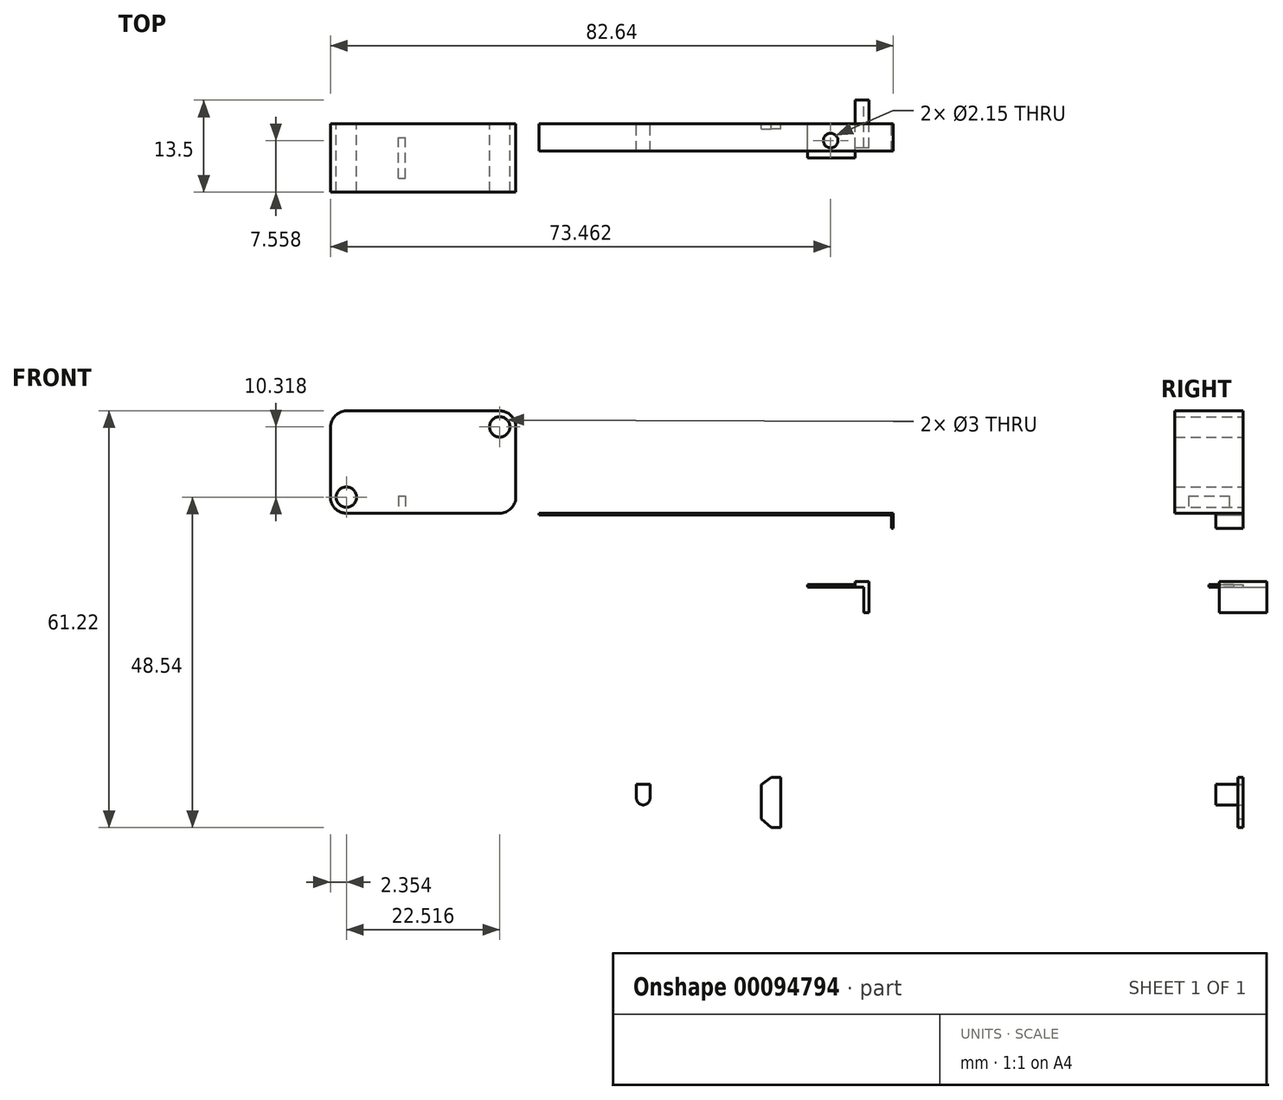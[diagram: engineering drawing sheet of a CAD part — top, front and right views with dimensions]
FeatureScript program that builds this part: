
annotation { "Feature Type Name" : "Feature", "Feature Type Description" : "" }
export const myFeature = defineFeature(function(context is Context, id is Id, definition is map)
    precondition{}
    {
        {
            var Q0;
            Q0=qCreatedBy(makeId("Front.planeOp"),FACE);
            var sketch = newSketch(context, id + "F0", { "sketchPlane" : qUnion([Q0])});
            skCircle(sketch, "E0", {"center": v(-20.95, 13.42) * mm, "radius": 2.36 * mm});
            skCircle(sketch, "E1", {"center": v(1.53, 13.43) * mm, "radius": 2.36 * mm});
            skCircle(sketch, "E2", {"center": v(-20.99, 3.11) * mm, "radius": 2.36 * mm});
            skCircle(sketch, "E3", {"center": v(1.53, 3.11) * mm, "radius": 2.36 * mm});
            skLineSegment(sketch, "E4", {"start": v(-31.54, 13.42) * mm, "end": v(17.5, 13.43) * mm, "construction": true});
            skLineSegment(sketch, "E5", {"start": v(-32, 3.11) * mm, "end": v(17.5, 3.11) * mm, "construction": true});
            skLineSegment(sketch, "E6", {"start": v(17.5, 3.11) * mm, "end": v(18.44, 4.02) * mm, "construction": true});
            skLineSegment(sketch, "E7", {"start": v(-23.3, 13.42) * mm, "end": v(-23.34, 3.11) * mm});
            skLineSegment(sketch, "E8", {"start": v(3.89, 13.43) * mm, "end": v(3.89, 3.11) * mm});
            skLineSegment(sketch, "E9", {"start": v(-20.95, 15.77) * mm, "end": v(1.53, 15.79) * mm});
            skLineSegment(sketch, "E10", {"start": v(-20.99, 0.75) * mm, "end": v(1.53, 0.75) * mm});
            skSolve(sketch);
        }
        {
            var Q0;
            Q0 = qSketchRegion(id + "F0", true);
            extrude(context, id + "F1", {"entities" : qUnion([Q0]), "depth" : 10 * mm});
        }
        {
            var Q0;
            Q0=makeQuery(id+"F1.opExtrude","CAP_FACE",FACE,{"disambiguationData":[OSD([sQuery(id+"F0.wireOp",EDGE,"E0"),sQuery(id+"F0.wireOp",EDGE,"E1"),sQuery(id+"F0.wireOp",EDGE,"E2"),sQuery(id+"F0.wireOp",EDGE,"E3"),sQuery(id+"F0.wireOp",EDGE,"E7"),sQuery(id+"F0.wireOp",EDGE,"E8"),sQuery(id+"F0.wireOp",EDGE,"E9"),sQuery(id+"F0.wireOp",EDGE,"E10")])],"isStart":true});
            var sketch = newSketch(context, id + "F2", { "sketchPlane" : qUnion([Q0])});
            skCircle(sketch, "E11", {"center": v(-1.53, 13.43) * mm, "radius": 1.5 * mm});
            skCircle(sketch, "E12", {"center": v(20.99, 3.11) * mm, "radius": 1.5 * mm});
            skSolve(sketch);
        }
        {
            var Q0;
            Q0 = qSketchRegion(id + "F2", true);
            extrude(context, id + "F3", {"entities" : qUnion([Q0]), "operationType" : NewBodyOperationType.REMOVE, "endBound" : BoundingType.THROUGH_ALL, "oppositeDirection" : true, "depth" : 25.4 * mm});
        }
        {
            var Q0;
            Q0=makeQuery(id+"F1.opExtrude","SWEPT_FACE",FACE,{"disambiguationData":[OSD([sQuery(id+"F0.wireOp",EDGE,"E10")])]});
            var sketch = newSketch(context, id + "F4", { "sketchPlane" : qUnion([Q0])});
            skLineSegment(sketch, "E13.bottom", {"start": v(-13.34, 8) * mm, "end": v(-12.34, 8) * mm});
            skLineSegment(sketch, "E13.top", {"start": v(-13.34, 2) * mm, "end": v(-12.34, 2) * mm});
            skLineSegment(sketch, "E13.left", {"start": v(-13.34, 8) * mm, "end": v(-13.34, 2) * mm});
            skLineSegment(sketch, "E13.right", {"start": v(-12.34, 8) * mm, "end": v(-12.34, 2) * mm});
            skSolve(sketch);
        }
        {
            var Q0;
            Q0 = qSketchRegion(id + "F4", true);
            extrude(context, id + "F5", {"entities" : qUnion([Q0]), "operationType" : NewBodyOperationType.REMOVE, "oppositeDirection" : true, "depth" : 2.5 * mm});
        }
        {
            var Q0;
            Q0=qCreatedBy(makeId("Front.planeOp"),FACE);
            var sketch = newSketch(context, id + "F6", { "sketchPlane" : qUnion([Q0])});
            skLineSegment(sketch, "E14.bottom", {"start": v(59.3, 0.5) * mm, "end": v(59.05, 0.5) * mm});
            skLineSegment(sketch, "E14.top", {"start": v(59.3, -1.5) * mm, "end": v(59.05, -1.5) * mm});
            skLineSegment(sketch, "E14.left", {"start": v(59.3, 0.5) * mm, "end": v(59.3, -1.5) * mm});
            skLineSegment(sketch, "E14.right", {"start": v(59.05, 0.5) * mm, "end": v(59.05, -1.5) * mm});
            skLineSegment(sketch, "E15.bottom", {"start": v(59.3, 0.5) * mm, "end": v(7.3, 0.5) * mm});
            skLineSegment(sketch, "E15.top", {"start": v(59.3, 0.75) * mm, "end": v(7.3, 0.75) * mm});
            skLineSegment(sketch, "E15.left", {"start": v(59.3, 0.5) * mm, "end": v(59.3, 0.75) * mm});
            skLineSegment(sketch, "E15.right", {"start": v(7.3, 0.5) * mm, "end": v(7.3, 0.75) * mm});
            skSolve(sketch);
        }
        {
            var Q0;
            Q0 = qSketchRegion(id + "F6", true);
            extrude(context, id + "F7", {"entities" : qUnion([Q0]), "depth" : 4 * mm});
        }
        {
            var Q0;
            Q0=qCreatedBy(makeId("Front.planeOp"),FACE);
            var sketch = newSketch(context, id + "F8", { "sketchPlane" : qUnion([Q0])});
            skLineSegment(sketch, "E16.bottom", {"start": v(55.72, -10.1) * mm, "end": v(54.97, -10.1) * mm});
            skLineSegment(sketch, "E16.top", {"start": v(55.72, -13.85) * mm, "end": v(54.97, -13.85) * mm});
            skLineSegment(sketch, "E16.left", {"start": v(55.72, -10.1) * mm, "end": v(55.72, -13.85) * mm});
            skLineSegment(sketch, "E16.right", {"start": v(54.97, -10.1) * mm, "end": v(54.97, -13.85) * mm});
            skLineSegment(sketch, "E17.bottom", {"start": v(55.72, -10.1) * mm, "end": v(53.72, -10.1) * mm});
            skLineSegment(sketch, "E17.top", {"start": v(55.72, -9.31) * mm, "end": v(53.72, -9.31) * mm});
            skLineSegment(sketch, "E17.left", {"start": v(55.72, -10.1) * mm, "end": v(55.72, -9.31) * mm});
            skLineSegment(sketch, "E17.right", {"start": v(53.72, -10.1) * mm, "end": v(53.72, -9.31) * mm});
            skLineSegment(sketch, "E18.bottom", {"start": v(53.72, -9.7) * mm, "end": v(46.72, -9.7) * mm});
            skLineSegment(sketch, "E18.top", {"start": v(53.72, -10.09) * mm, "end": v(46.72, -10.09) * mm});
            skLineSegment(sketch, "E18.left", {"start": v(53.72, -9.7) * mm, "end": v(53.72, -10.09) * mm});
            skLineSegment(sketch, "E18.right", {"start": v(46.72, -9.7) * mm, "end": v(46.72, -10.09) * mm});
            skSolve(sketch);
        }
        {
            var Q0;
            {var subQ0=sQuery(id+"F8.wireOp",EDGE,"E17.top");Q0=makeQuery(id+"F8.imprint","IMPRINT",FACE,{"disambiguationData":[TD([[makeQuery(id+"F8.imprint","IMPRINT",EDGE,{"derivedFrom":subQ0}),1.0]])]});}
            var Q1;
            Q1=makeQuery(id+"F8.imprint","IMPRINT",FACE,{"disambiguationData":[TD([[makeQuery(id+"F8.imprint","IMPRINT",EDGE,{"derivedFrom":sQuery(id+"F8.wireOp",EDGE,"E16.top")}),-1.0]])]});
            extrude(context, id + "F9", {"entities" : qUnion([Q0, Q1]), "endBound" : BoundingType.SYMMETRIC, "depth" : 7 * mm});
        }
        {
            var Q0;
            Q0=makeQuery(id+"F8.imprint","IMPRINT",FACE,{"disambiguationData":[TD([[makeQuery(id+"F8.imprint","IMPRINT",EDGE,{"derivedFrom":sQuery(id+"F8.wireOp",EDGE,"E18.bottom")}),1.0]])]});
            extrude(context, id + "F10", {"entities" : qUnion([Q0]), "operationType" : NewBodyOperationType.ADD, "depth" : 5 * mm});
        }
        {
            var Q0;
            Q0=makeQuery(id+"F10.opExtrude","SWEPT_FACE",FACE,{"disambiguationData":[OSD([sQuery(id+"F8.wireOp",EDGE,"E18.top")])]});
            var sketch = newSketch(context, id + "F11", { "sketchPlane" : qUnion([Q0])});
            skCircle(sketch, "E19", {"center": v(50.12, 2.44) * mm, "radius": 1.08 * mm});
            skSolve(sketch);
        }
        {
            var Q0;
            Q0 = qSketchRegion(id + "F11", true);
            extrude(context, id + "F12", {"entities" : qUnion([Q0]), "operationType" : NewBodyOperationType.REMOVE, "endBound" : BoundingType.THROUGH_ALL, "oppositeDirection" : true, "depth" : 25.4 * mm});
        }
        {
            var Q0;
            Q0=qCreatedBy(makeId("Front.planeOp"),FACE);
            var sketch = newSketch(context, id + "F13", { "sketchPlane" : qUnion([Q0])});
            skLineSegment(sketch, "E20.bottom", {"start": v(42.81, -45.43) * mm, "end": v(39.95, -45.43) * mm});
            skLineSegment(sketch, "E20.top", {"start": v(42.81, -38.05) * mm, "end": v(39.95, -38.05) * mm});
            skLineSegment(sketch, "E20.left", {"start": v(42.81, -45.43) * mm, "end": v(42.81, -38.05) * mm});
            skLineSegment(sketch, "E20.right", {"start": v(39.95, -45.43) * mm, "end": v(39.95, -38.05) * mm});
            skLineSegment(sketch, "E21.bottom", {"start": v(39.95, -44.16) * mm, "end": v(32.1, -44.16) * mm});
            skLineSegment(sketch, "E21.top", {"start": v(39.95, -39.16) * mm, "end": v(32.1, -39.16) * mm});
            skLineSegment(sketch, "E21.left", {"start": v(39.95, -44.16) * mm, "end": v(39.95, -39.16) * mm});
            skLineSegment(sketch, "E21.right", {"start": v(32.1, -44.16) * mm, "end": v(32.1, -39.16) * mm});
            skLineSegment(sketch, "E22", {"start": v(39.95, -44.16) * mm, "end": v(41.38, -45.43) * mm});
            skLineSegment(sketch, "E23", {"start": v(39.95, -39.16) * mm, "end": v(41.38, -38.05) * mm});
            skLineSegment(sketch, "E24", {"start": v(32.1, -43.13) * mm, "end": v(33.53, -44.16) * mm});
            skLineSegment(sketch, "E25", {"start": v(32.1, -40.35) * mm, "end": v(33.37, -39.16) * mm});
            skSolve(sketch);
        }
        {
            var Q0;
            {var subQ0=sQuery(id+"F13.wireOp",EDGE,"E20.left");Q0=makeQuery(id+"F13.imprint","IMPRINT",FACE,{"disambiguationData":[TD([[makeQuery(id+"F13.imprint","IMPRINT",EDGE,{"derivedFrom":subQ0}),1.0]])]});}
            var Q1;
            {var subQ3=sQuery(id+"F13.wireOp",EDGE,"E21.left");Q1=makeQuery(id+"F13.imprint","IMPRINT",FACE,{"disambiguationData":[TD([[makeQuery(id+"F13.imprint","IMPRINT",EDGE,{"derivedFrom":subQ3}),1.0]])]});}
            extrude(context, id + "F14", {"entities" : qUnion([Q0, Q1]), "depth" : .75 * mm});
        }
        {
            var Q0;
            Q0=makeQuery(id+"F14.opExtrude","CAP_FACE",FACE,{"disambiguationData":[OSD([sQuery(id+"F13.wireOp",EDGE,"E20.bottom"),sQuery(id+"F13.wireOp",EDGE,"E20.top"),sQuery(id+"F13.wireOp",EDGE,"E20.left"),sQuery(id+"F13.wireOp",EDGE,"E21.bottom"),sQuery(id+"F13.wireOp",EDGE,"E21.top"),sQuery(id+"F13.wireOp",EDGE,"E21.right"),sQuery(id+"F13.wireOp",EDGE,"E22"),sQuery(id+"F13.wireOp",EDGE,"E23"),sQuery(id+"F13.wireOp",EDGE,"E24"),sQuery(id+"F13.wireOp",EDGE,"E25")])],"isStart":false});
            var sketch = newSketch(context, id + "F15", { "sketchPlane" : qUnion([Q0])});
            skCircle(sketch, "E26", {"center": v(36.92, -41.66) * mm, "radius": 1.39 * mm});
            skSolve(sketch);
        }
        {
            var Q0;
            Q0=makeQuery(id+"F15.imprint","IMPRINT",FACE,{"disambiguationData":[TD([[makeQuery(id+"F15.imprint","IMPRINT",EDGE,{"derivedFrom":sQuery(id+"F15.wireOp",EDGE,"E26")}),1.0]])]});
            extrude(context, id + "F16", {"entities" : qUnion([Q0]), "operationType" : NewBodyOperationType.REMOVE, "endBound" : BoundingType.THROUGH_ALL, "oppositeDirection" : true, "depth" : 25.4 * mm});
        }
        {
            var Q0;
            Q0=qCreatedBy(makeId("Front.planeOp"),FACE);
            var sketch = newSketch(context, id + "F17", { "sketchPlane" : qUnion([Q0])});
            skCircle(sketch, "E27", {"center": v(22.6, -41.1) * mm, "radius": 1 * mm});
            skLineSegment(sketch, "E28", {"start": v(23.6, -41.1) * mm, "end": v(23.6, -39.1) * mm});
            skLineSegment(sketch, "E29", {"start": v(21.6, -41.1) * mm, "end": v(21.6, -39.1) * mm});
            skLineSegment(sketch, "E30", {"start": v(21.6, -39.1) * mm, "end": v(23.6, -39.1) * mm});
            skSolve(sketch);
        }
        {
            var Q0;
            Q0 = qSketchRegion(id + "F17", true);
            extrude(context, id + "F18", {"entities" : qUnion([Q0]), "depth" : 4 * mm});
        }
    });
